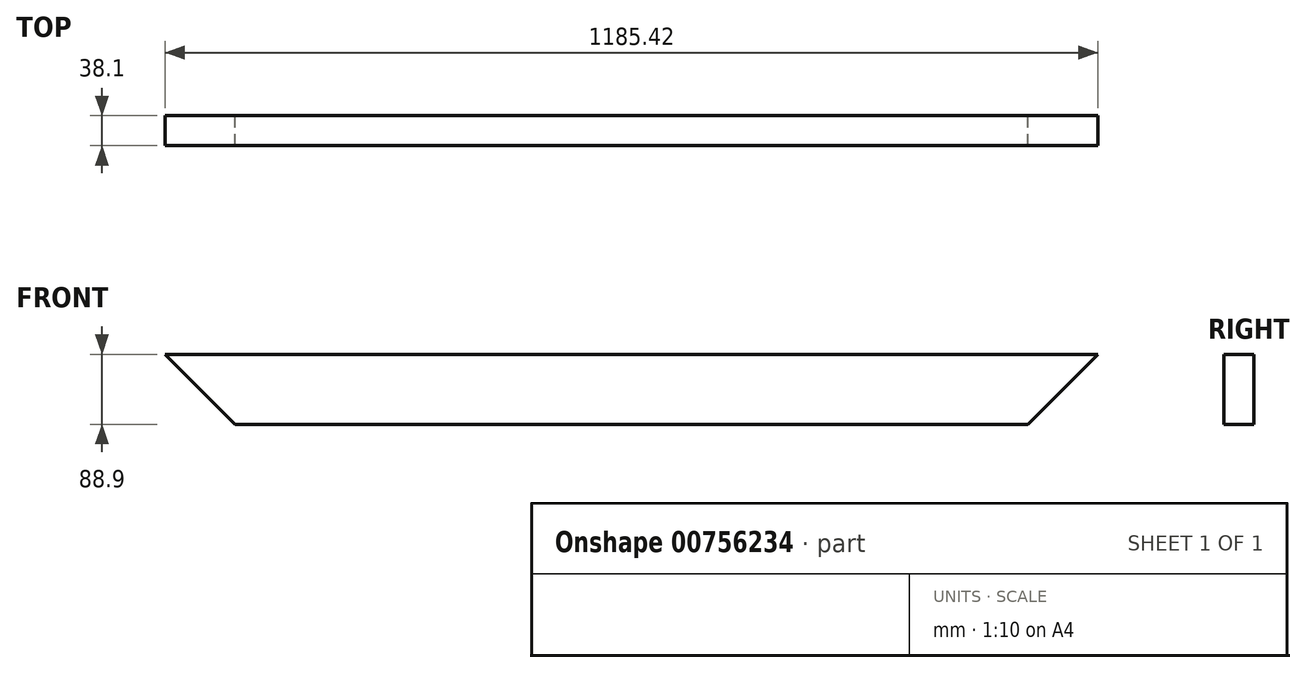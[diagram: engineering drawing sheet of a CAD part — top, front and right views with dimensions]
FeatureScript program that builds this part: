
annotation { "Feature Type Name" : "Feature", "Feature Type Description" : "" }
export const myFeature = defineFeature(function(context is Context, id is Id, definition is map)
    precondition{}
    {
        {
            var Q0;
            Q0=qCreatedBy(makeId("Front.planeOp"),FACE);
            var sketch = newSketch(context, id + "F0", { "sketchPlane" : qUnion([Q0])});
            skLineSegment(sketch, "E0.bottom", {"start": v(-592.7, 44.45) * mm, "end": v(592.7, 44.45) * mm});
            skLineSegment(sketch, "E0.top", {"start": v(-592.7, -44.45) * mm, "end": v(592.7, -44.45) * mm});
            skLineSegment(sketch, "E0.left", {"start": v(-592.7, 44.45) * mm, "end": v(-592.7, -44.45) * mm});
            skLineSegment(sketch, "E0.right", {"start": v(592.7, 44.45) * mm, "end": v(592.7, -44.45) * mm});
            skPoint(sketch, "E0.middle", {"position": v(0, 0) * mm});
            skLineSegment(sketch, "E1.bottom", {"start": v(-592.7, -44.45) * mm, "end": v(-503.8, -44.45) * mm});
            skLineSegment(sketch, "E1.top", {"start": v(-592.7, 44.45) * mm, "end": v(-503.8, 44.45) * mm});
            skLineSegment(sketch, "E2", {"start": v(-592.7, 44.45) * mm, "end": v(-503.8, -44.45) * mm});
            skLineSegment(sketch, "E3", {"start": v(592.7, 44.45) * mm, "end": v(503.8, -44.45) * mm});
            skSolve(sketch);
        }
        {
            var Q0;
            Q0=makeQuery(id+"F0.imprint","IMPRINT",FACE,{"disambiguationData":[TD([[makeQuery(id+"F0.imprint","IMPRINT",EDGE,{"derivedFrom":sQuery(id+"F0.wireOp",EDGE,"E0.bottom")}),-1.0]])]});
            extrude(context, id + "F1", {"entities" : qUnion([Q0]), "endBound" : BoundingType.SYMMETRIC, "depth" : 38.1 * mm, "offsetDistance" : 25.4 * mm});
        }
    });
